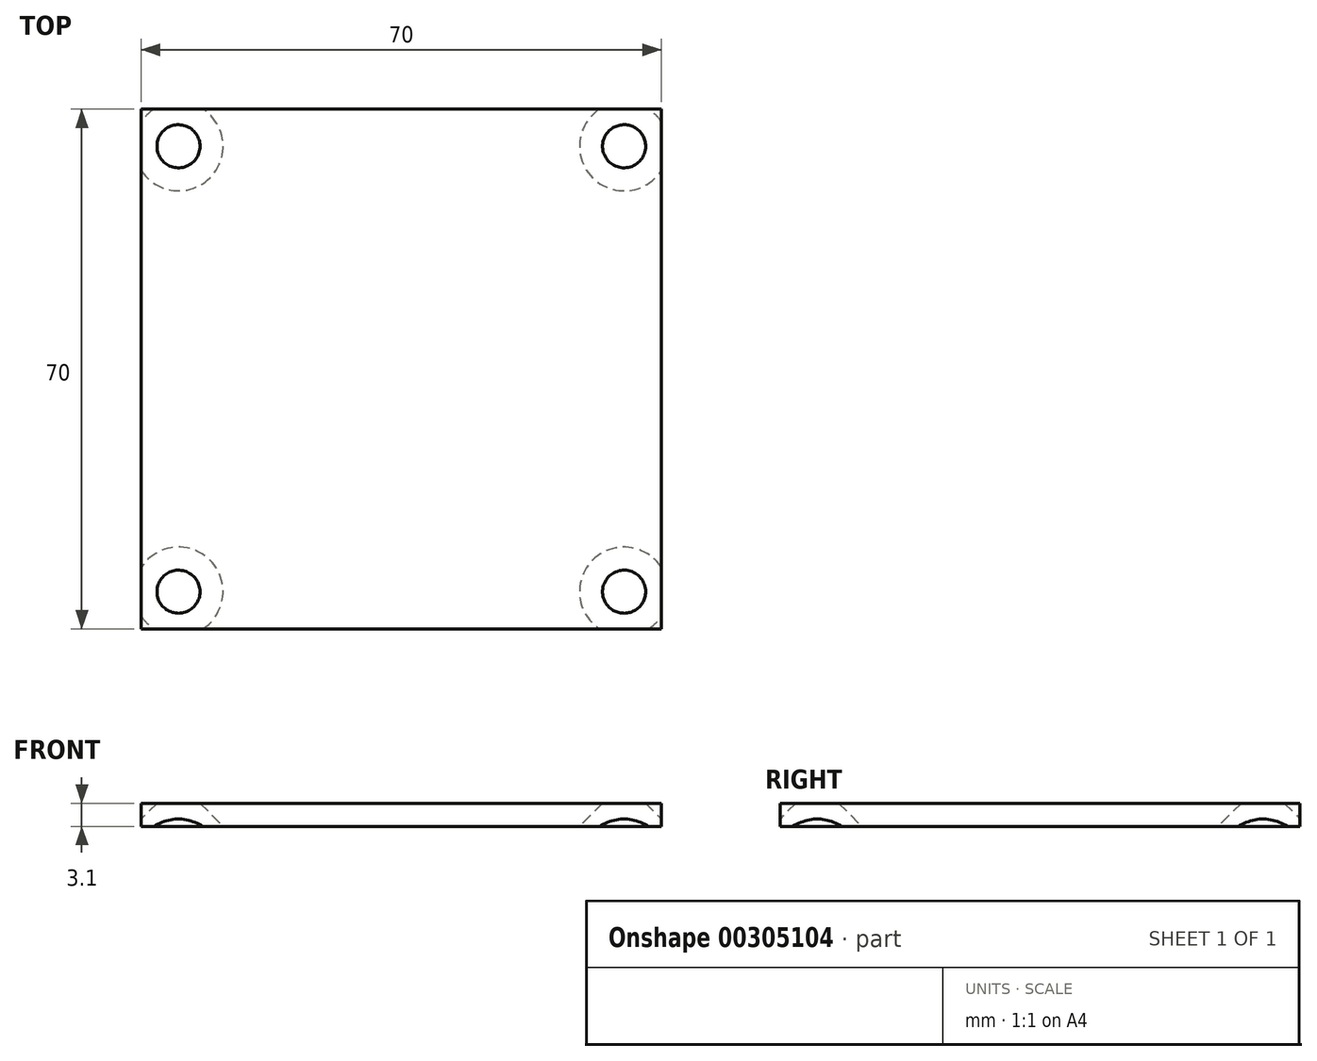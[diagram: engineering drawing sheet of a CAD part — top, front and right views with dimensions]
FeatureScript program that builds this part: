
annotation { "Feature Type Name" : "Feature", "Feature Type Description" : "" }
export const myFeature = defineFeature(function(context is Context, id is Id, definition is map)
    precondition{}
    {
        {
            var Q0;
            Q0=qCreatedBy(makeId("Top.planeOp"),FACE);
            var sketch = newSketch(context, id + "F0", { "sketchPlane" : qUnion([Q0])});
            skLineSegment(sketch, "E0.bottom", {"start": v(35, -35) * mm, "end": v(-35, -35) * mm});
            skLineSegment(sketch, "E0.top", {"start": v(35, 35) * mm, "end": v(-35, 35) * mm});
            skLineSegment(sketch, "E0.left", {"start": v(35, -35) * mm, "end": v(35, 35) * mm});
            skLineSegment(sketch, "E0.right", {"start": v(-35, -35) * mm, "end": v(-35, 35) * mm});
            skPoint(sketch, "E0.middle", {"position": v(0, 0) * mm});
            skLineSegment(sketch, "E1.bottom", {"start": v(-30, 30) * mm, "end": v(30, 30) * mm});
            skLineSegment(sketch, "E1.top", {"start": v(-30, -30) * mm, "end": v(30, -30) * mm});
            skLineSegment(sketch, "E1.left", {"start": v(-30, 30) * mm, "end": v(-30, -30) * mm});
            skLineSegment(sketch, "E1.right", {"start": v(30, 30) * mm, "end": v(30, -30) * mm});
            skSolve(sketch);
        }
        {
            var Q0;
            Q0 = qSketchRegion(id + "F0", true);
            var Q1;
            Q1=makeQuery(id+"F0.imprint","IMPRINT",FACE,{"disambiguationData":[TD([[makeQuery(id+"F0.imprint","IMPRINT",EDGE,{"derivedFrom":sQuery(id+"F0.wireOp",EDGE,"E1.bottom")}),-1.0]])]});
            extrude(context, id + "F1", {"entities" : qUnion([Q0, Q1]), "depth" : 3.1 * mm});
        }
        {
            var Q0;
            Q0=sQuery(id+"F0.wireOp",VERTEX,"E1.left.start");
            var Q1;
            Q1=sQuery(id+"F0.wireOp",VERTEX,"E1.bottom.end");
            var Q2;
            Q2=sQuery(id+"F0.wireOp",VERTEX,"E1.top.end");
            var Q3;
            Q3=sQuery(id+"F0.wireOp",VERTEX,"E1.top.start");
            var Q4;
            Q4=makeQuery(id+"F1.opExtrude","SWEPT_BODY",BODY,{"disambiguationData":[OSD([sQuery(id+"F0.wireOp",EDGE,"E0.bottom"),sQuery(id+"F0.wireOp",EDGE,"E0.top"),sQuery(id+"F0.wireOp",EDGE,"E0.left"),sQuery(id+"F0.wireOp",EDGE,"E0.right")])]});
            hole(context, id + "F2", {"style" : HoleStyle.C_SINK, "endStyle" : HoleEndStyle.BLIND, "oppositeDirection" : true, "standardTappedOrClearance" : lookupTablePath({ "standard" : "ISO", "size" : "4", "type" : "Drilled" }), "standardBlindInLast" : lookupTablePath({ "standard" : "ISO", "size" : "4", "type" : "Drilled" }), "holeDiameter" : 4 * mm, "cSinkDiameter" : 12 * mm, "cSinkAngle" : 90 * degree, "holeDepth" : 15 * mm, "isTappedThrough" : true, "tappedDepth" : 12 * mm, "tapClearance" : 3, "locations" : qUnion([Q0, Q1, Q2, Q3]), "scope" : qUnion([Q4]), "startStyle" : HoleStartStyle.SKETCH});
        }
    });
